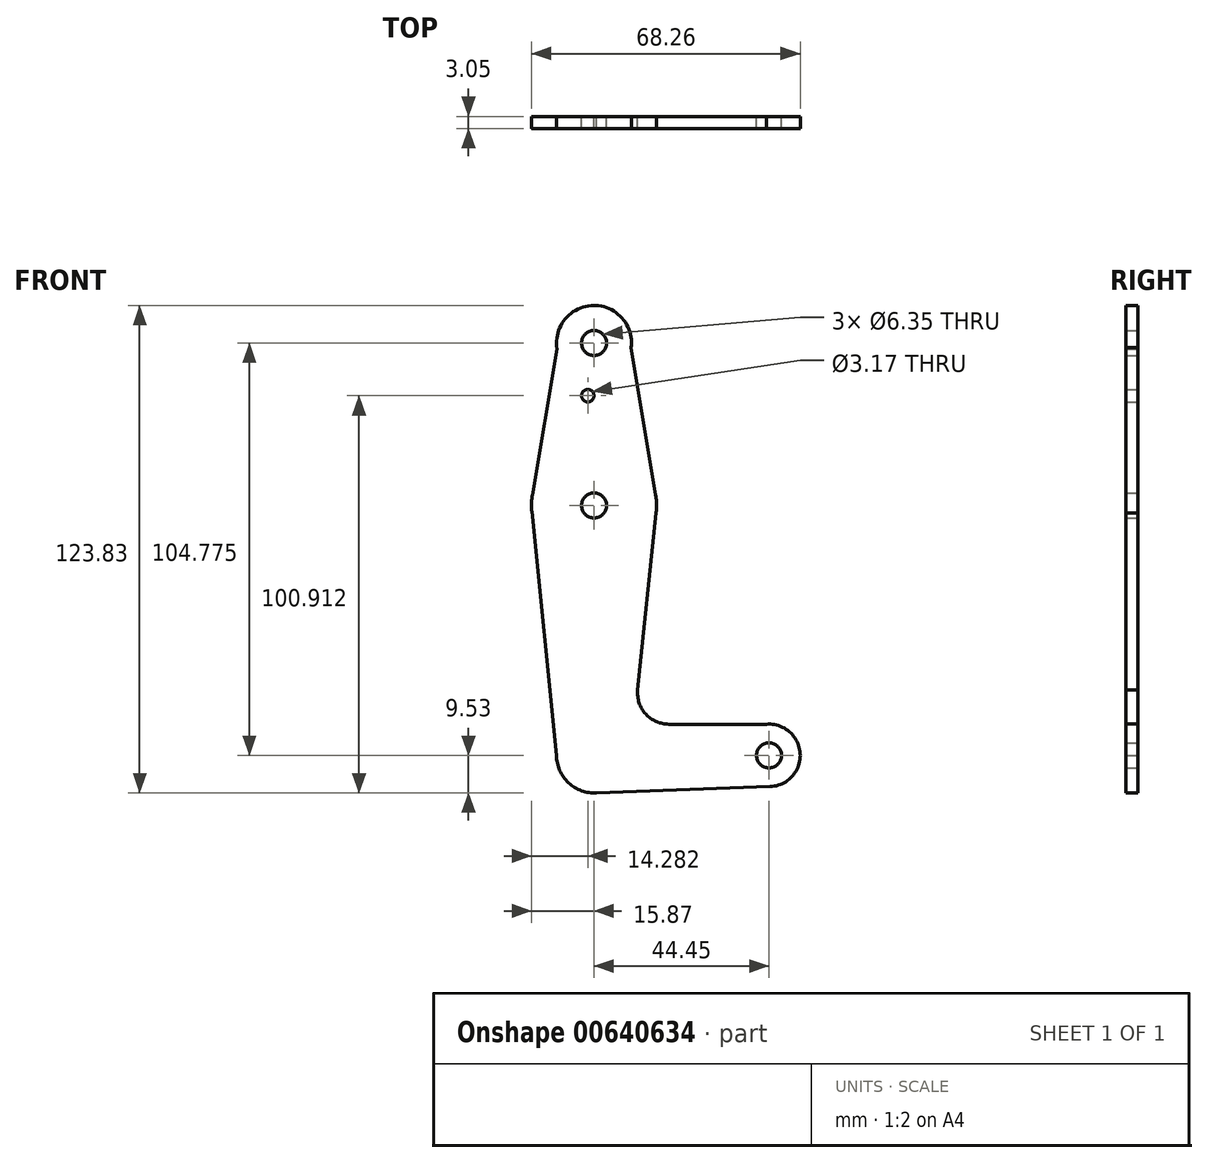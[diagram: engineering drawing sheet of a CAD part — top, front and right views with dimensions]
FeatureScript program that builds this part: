
annotation { "Feature Type Name" : "Feature", "Feature Type Description" : "" }
export const myFeature = defineFeature(function(context is Context, id is Id, definition is map)
    precondition{}
    {
        {
            var Q0;
            Q0=qCreatedBy(makeId("Front.planeOp"),FACE);
            var sketch = newSketch(context, id + "F0", { "sketchPlane" : qUnion([Q0])});
            skLineSegment(sketch, "E0", {"start": v(0, 0) * mm, "end": v(44.45, 0) * mm});
            skLineSegment(sketch, "E1", {"start": v(44.45, 0) * mm, "end": v(0, 0) * mm, "construction": true});
            skLineSegment(sketch, "E2", {"start": v(0, 104.78) * mm, "end": v(0, 0) * mm, "construction": true});
            skCircle(sketch, "E3", {"center": v(0, 104.78) * mm, "radius": 9.53 * mm});
            skCircle(sketch, "E4", {"center": v(0, 0) * mm, "radius": 9.53 * mm});
            skCircle(sketch, "E5", {"center": v(44.45, 0) * mm, "radius": 7.94 * mm});
            skCircle(sketch, "E6", {"center": v(0, 63.5) * mm, "radius": 15.88 * mm});
            skLineSegment(sketch, "E7", {"start": v(-8.39, 109.3) * mm, "end": v(-15.65, 66.14) * mm});
            skLineSegment(sketch, "E8", {"start": v(8.55, 108.98) * mm, "end": v(15.66, 66.1) * mm});
            skLineSegment(sketch, "E9", {"start": v(0, -9.53) * mm, "end": v(44.73, -7.93) * mm});
            skLineSegment(sketch, "E10", {"start": v(43.78, 7.9) * mm, "end": v(19.01, 7.9) * mm});
            skPoint(sketch, "E11.visualSharp", {"position": v(10.3, 7.9) * mm});
            skArc(sketch, "E11.filletArc", {"start": v(11.1, 16.59) * mm, "mid": v(13.14, 10.5) * mm, "end": v(19.01, 7.9) * mm});
            skCircle(sketch, "E12", {"center": v(-1.59, 91.38) * mm, "radius": 1.59 * mm});
            skCircle(sketch, "E13", {"center": v(0, 104.78) * mm, "radius": 3.18 * mm});
            skCircle(sketch, "E14", {"center": v(44.45, 0) * mm, "radius": 3.18 * mm});
            skCircle(sketch, "E15", {"center": v(0, 63.5) * mm, "radius": 3.18 * mm});
            skLineSegment(sketch, "E16", {"start": v(15.75, 61.55) * mm, "end": v(11.1, 16.59) * mm});
            skLineSegment(sketch, "E17", {"start": v(-9.52, 0) * mm, "end": v(-15.8, 61.9) * mm});
            skSolve(sketch);
        }
        {
            var Q0;
            Q0 = qSketchRegion(id + "F0", true);
            extrude(context, id + "F1", {"entities" : qUnion([Q0]), "depth" : 3.05 * mm, "offsetDistance" : 25.4 * mm});
        }
    });
